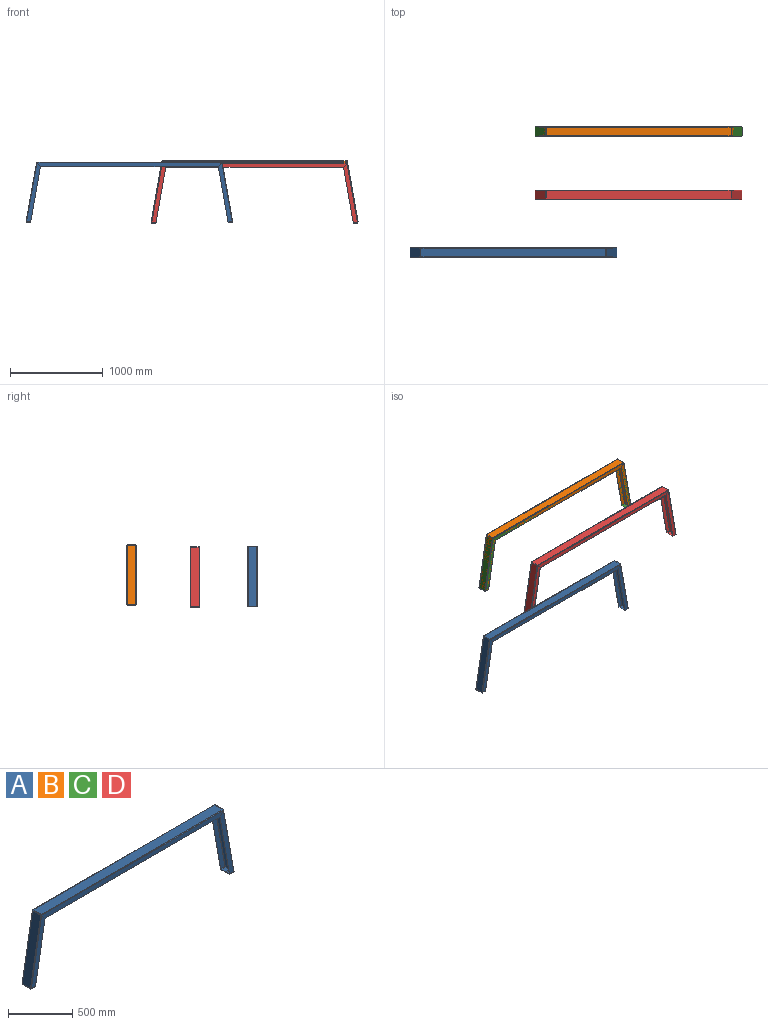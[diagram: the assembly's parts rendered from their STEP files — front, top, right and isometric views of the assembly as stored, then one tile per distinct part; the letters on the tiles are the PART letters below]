
ASSEMBLY  parts=4 mates=1
PART A: 130 faces, bbox 2234.1x100x650 mm
  f0: plane 3.37x2.87mm, normal (0,1,0), area 7.2mm2, adj f5,f11,f12,f83
  f1: plane 2.96x0.53mm, normal (0,-1,0), area 0mm2, adj f11,f12,f13,f75
  f2: plane 3.37x2.87mm, normal (0,-1,0), area 7.2mm2, adj f42,f48,f49,f66
  f3: plane 2.96x0.53mm, normal (0,1,0), area 0mm2, adj f48,f49,f51,f58
  f4: plane 2.95x2mm, normal (-0.17,0,0.98), area 6mm2, adj f8,f9,f11,f12
  f5: plane 2.95x2mm, normal (-0.17,0,0.98), area 6mm2, adj f0,f6,f11,f12
  f6: plane 3.52x3.48mm, normal (0,1,0), area 9.1mm2, adj f5,f10,f11,f12
  f7: plane 2.96x0.53mm, normal (0,1,0), area 0mm2, adj f11,f12,f14,f82
  f8: plane 3.37x2.87mm, normal (0,-1,0), area 7.2mm2, adj f4,f11,f12,f74
  f9: plane 3.52x3.48mm, normal (0,-1,0), area 9.1mm2, adj f4,f10,f11,f12
  f10: plane 94x2.95mm, normal (0.17,0,-0.98), area 282mm2, adj f6,f9,f11,f12
  f11: plane 645.35x113.79mm, normal (0.98,0,0.17), area 58989.4mm2, adj f0,f1,f4,f5,f6,f7,f8,f9
  f12: plane 645.35x113.79mm, normal (-0.98,0,-0.17), area 58989.4mm2, adj f0,f1,f4,f5,f6,f7,f8,f9
  f13: plane 4.92x4.65mm, normal (0,-1,0), area 14.7mm2, adj f1,f15,f16,f20
  f14: plane 4.92x4.65mm, normal (0,1,0), area 14.7mm2, adj f7,f15,f16,f17
  f15: cylinder r=5mm len=90mm, axis (0,-1,0), area 628.3mm2, adj f11,f13,f14,f21
  f16: cylinder r=2mm len=90mm, axis (0,-1,0), area 251.3mm2, adj f12,f13,f14,f22
  f17: plane 3x0.01mm, normal (0,1,0), area 0mm2, adj f14,f21,f22,f33
  f18: plane 3x0.01mm, normal (0,-1,0), area 0mm2, adj f21,f22,f29,f50
  f19: plane 3x0.01mm, normal (0,1,0), area 0mm2, adj f21,f22,f32,f51
  f20: plane 3x0.01mm, normal (0,-1,0), area 0mm2, adj f13,f21,f22,f28
  f21: plane 1996.64x90mm, normal (0,0,1), area 179697.9mm2, adj f15,f17,f18,f19,f20,f30,f34,f52
  f22: plane 1996.64x90mm, normal (0,0,-1), area 179697.9mm2, adj f16,f17,f18,f19,f20,f31,f35,f53
  f23: plane 1921.1x3mm, normal (0,0,-1), area 5763.3mm2, adj f24,f25,f26,f27
  f24: plane 45x37.76mm, normal (0.77,0,-0.64), area 176.2mm2, adj f23,f26,f27,f28
  f25: plane 45x37.76mm, normal (-0.77,0,-0.64), area 176.2mm2, adj f23,f26,f27,f29
  f26: plane 1996.62x45mm, normal (0,-1,0), area 88148.6mm2, adj f23,f24,f25,f30
  f27: plane 1996.62x45mm, normal (0,1,0), area 88148.6mm2, adj f23,f24,f25,f31
  f28: plane 5x5mm, normal (1,0,0), area 16.5mm2, adj f20,f24,f30,f31
  f29: plane 5x5mm, normal (-1,0,0), area 16.5mm2, adj f18,f25,f30,f31
  f30: cylinder r=5mm len=1996.62mm, axis (1,0,0), area 15681.4mm2, adj f21,f26,f28,f29
  f31: cylinder r=2mm len=1996.62mm, axis (1,0,0), area 6272.6mm2, adj f22,f27,f28,f29
  f32: plane 5x5mm, normal (-1,0,0), area 16.5mm2, adj f19,f34,f35,f37
  f33: plane 5x5mm, normal (1,0,0), area 16.5mm2, adj f17,f34,f35,f38
  f34: cylinder r=5mm len=1996.62mm, axis (-1,0,0), area 15681.4mm2, adj f21,f32,f33,f39
  f35: cylinder r=2mm len=1996.62mm, axis (-1,0,0), area 6272.6mm2, adj f22,f32,f33,f40
  f36: plane 1921.1x3mm, normal (0,0,-1), area 5763.3mm2, adj f37,f38,f39,f40
  f37: plane 45x37.76mm, normal (-0.77,0,-0.64), area 176.2mm2, adj f32,f36,f39,f40
  f38: plane 45x37.76mm, normal (0.77,0,-0.64), area 176.2mm2, adj f33,f36,f39,f40
  f39: plane 1996.62x45mm, normal (0,1,0), area 88148.6mm2, adj f34,f36,f37,f38
  f40: plane 1996.62x45mm, normal (0,-1,0), area 88148.6mm2, adj f35,f36,f37,f38
  f41: plane 2.95x2mm, normal (0.17,0,0.98), area 6mm2, adj f46,f47,f48,f49
  f42: plane 2.95x2mm, normal (0.17,0,0.98), area 6mm2, adj f2,f44,f48,f49
  f43: plane 94x2.95mm, normal (-0.17,0,-0.98), area 282mm2, adj f44,f47,f48,f49
  f44: plane 3.52x3.48mm, normal (0,-1,0), area 9.1mm2, adj f42,f43,f48,f49
  f45: plane 2.96x0.53mm, normal (0,-1,0), area 0mm2, adj f48,f49,f50,f67
  f46: plane 3.37x2.87mm, normal (0,1,0), area 7.2mm2, adj f41,f48,f49,f59
  f47: plane 3.52x3.48mm, normal (0,1,0), area 9.1mm2, adj f41,f43,f48,f49
  f48: plane 645.35x113.79mm, normal (-0.98,0,0.17), area 58989.4mm2, adj f2,f3,f41,f42,f43,f44,f45,f46
  f49: plane 645.35x113.79mm, normal (0.98,0,-0.17), area 58989.4mm2, adj f2,f3,f41,f42,f43,f44,f45,f46
  f50: plane 4.92x4.65mm, normal (0,-1,0), area 14.7mm2, adj f18,f45,f52,f53
  f51: plane 4.92x4.65mm, normal (0,1,0), area 14.7mm2, adj f3,f19,f52,f53
  f52: cylinder r=5mm len=90mm, axis (0,-1,0), area 628.3mm2, adj f21,f48,f50,f51
  f53: cylinder r=2mm len=90mm, axis (0,-1,0), area 251.3mm2, adj f22,f49,f50,f51
  f54: plane 45x37.76mm, normal (0.77,0,0.64), area 176.2mm2, adj f55,f56,f57,f58
  f55: plane 594.99x104.91mm, normal (0.98,0,-0.17), area 1812.5mm2, adj f54,f56,f57,f105
  f56: plane 639.99x150.61mm, normal (0,1,0), area 28215.6mm2, adj f54,f55,f60,f106
  f57: plane 639.99x150.61mm, normal (0,-1,0), area 28215.6mm2, adj f54,f55,f61,f107
  f58: plane 5x4.92mm, normal (0.17,0,0.98), area 16.5mm2, adj f3,f54,f60,f61
  f59: plane 5x4.92mm, normal (-0.17,0,-0.98), area 16.5mm2, adj f46,f60,f61,f104
  f60: cylinder r=5mm len=640.86mm, axis (0.17,0,0.98), area 5104mm2, adj f48,f56,f58,f59
  f61: cylinder r=2mm len=640.33mm, axis (0.17,0,0.98), area 2041.6mm2, adj f49,f57,f58,f59
  f62: plane 594.99x104.91mm, normal (0.98,0,-0.17), area 1812.5mm2, adj f63,f64,f65,f126
  f63: plane 45x37.76mm, normal (0.77,0,0.64), area 176.2mm2, adj f62,f64,f65,f67
  f64: plane 639.99x150.61mm, normal (0,-1,0), area 28215.6mm2, adj f62,f63,f68,f128
  f65: plane 639.99x150.61mm, normal (0,1,0), area 28215.6mm2, adj f62,f63,f69,f129
  f66: plane 5x4.92mm, normal (-0.17,0,-0.98), area 16.5mm2, adj f2,f68,f69,f127
  f67: plane 5x4.92mm, normal (0.17,0,0.98), area 16.5mm2, adj f45,f63,f68,f69
  f68: cylinder r=5mm len=640.86mm, axis (-0.17,0,-0.98), area 5104mm2, adj f48,f64,f66,f67
  f69: cylinder r=2mm len=640.33mm, axis (-0.17,0,-0.98), area 2041.6mm2, adj f49,f65,f66,f67
  f70: plane 45x37.76mm, normal (-0.77,0,0.64), area 176.2mm2, adj f71,f72,f73,f75
  f71: plane 594.99x104.91mm, normal (-0.98,0,-0.17), area 1812.5mm2, adj f70,f72,f73,f114
  f72: plane 639.99x150.61mm, normal (0,-1,0), area 28215.6mm2, adj f70,f71,f76,f115
  f73: plane 639.99x150.61mm, normal (0,1,0), area 28215.6mm2, adj f70,f71,f77,f116
  f74: plane 5x4.92mm, normal (0.17,0,-0.98), area 16.5mm2, adj f8,f76,f77,f113
  f75: plane 5x4.92mm, normal (-0.17,0,0.98), area 16.5mm2, adj f1,f70,f76,f77
  f76: cylinder r=5mm len=640.86mm, axis (0.17,0,-0.98), area 5104mm2, adj f11,f72,f74,f75
  f77: cylinder r=2mm len=640.33mm, axis (0.17,0,-0.98), area 2041.6mm2, adj f12,f73,f74,f75
  f78: plane 594.99x104.91mm, normal (-0.98,0,-0.17), area 1812.5mm2, adj f79,f80,f81,f91
  f79: plane 45x37.76mm, normal (-0.77,0,0.64), area 176.2mm2, adj f78,f80,f81,f82
  f80: plane 639.99x150.61mm, normal (0,1,0), area 28215.6mm2, adj f78,f79,f84,f93
  f81: plane 639.99x150.61mm, normal (0,-1,0), area 28215.6mm2, adj f78,f79,f85,f94
  f82: plane 5x4.92mm, normal (-0.17,0,0.98), area 16.5mm2, adj f7,f79,f84,f85
  f83: plane 5x4.92mm, normal (0.17,0,-0.98), area 16.5mm2, adj f0,f84,f85,f92
  f84: cylinder r=5mm len=640.86mm, axis (-0.17,0,0.98), area 5104mm2, adj f11,f80,f82,f83
  f85: cylinder r=2mm len=640.33mm, axis (-0.17,0,0.98), area 2041.6mm2, adj f12,f81,f82,f83
  f86: plane 45.34x3mm, normal (0,-1,0), area 136mm2, adj f87,f88,f89,f90
  f87: plane 44.99x3mm, normal (-1,0,0), area 135mm2, adj f86,f89,f90,f91
  f88: plane 44.99x3mm, normal (1,0,0), area 135mm2, adj f86,f89,f90,f92
  f89: plane 45.34x44.99mm, normal (0,0,-1), area 2039.9mm2, adj f86,f87,f88,f93
  f90: plane 45.34x44.99mm, normal (0,0,1), area 2039.9mm2, adj f86,f87,f88,f94
  f91: bspline ~5x5mm, area 16.6mm2, adj f78,f87,f93,f94
  f92: plane 5x5mm, normal (1,0,0), area 16.5mm2, adj f83,f88,f93,f94
  f93: cylinder r=5mm len=45.69mm, axis (-1,0,0), area 357.5mm2, adj f80,f89,f91,f92
  f94: cylinder r=2mm len=45.69mm, axis (-1,0,0), area 143mm2, adj f81,f90,f91,f92
  f95: plane 10x3mm, normal (0,-1,0), area 30mm2, adj f96,f101,f102,f103
  f96: plane 10x3mm, normal (1,0,0), area 30mm2, adj f95,f97,f102,f103
  f97: plane 10x3mm, normal (0,1,0), area 30mm2, adj f96,f101,f102,f103
  f98: plane 45.34x3mm, normal (0,-1,0), area 136mm2, adj f99,f100,f102,f103
  f99: plane 44.99x3mm, normal (-1,0,0), area 135mm2, adj f98,f102,f103,f104
  f100: plane 44.99x3mm, normal (1,0,0), area 135mm2, adj f98,f102,f103,f105
  f101: plane 10x3mm, normal (-1,0,0), area 30mm2, adj f95,f97,f102,f103
  f102: plane 45.34x44.99mm, normal (0,0,-1), area 1939.9mm2, adj f95,f96,f97,f98,f99,f100,f101,f106
  f103: plane 45.34x44.99mm, normal (0,0,1), area 1939.9mm2, adj f95,f96,f97,f98,f99,f100,f101,f107
  f104: plane 5x5mm, normal (-1,0,0), area 16.5mm2, adj f59,f99,f106,f107
  f105: bspline ~5x5mm, area 16.6mm2, adj f55,f100,f106,f107
  f106: cylinder r=5mm len=45.69mm, axis (-1,0,0), area 357.5mm2, adj f56,f102,f104,f105
  f107: cylinder r=2mm len=45.69mm, axis (-1,0,0), area 143mm2, adj f57,f103,f104,f105
  f108: plane 45.34x3mm, normal (0,1,0), area 136mm2, adj f109,f110,f111,f112
  f109: plane 44.99x3mm, normal (1,0,0), area 135mm2, adj f108,f111,f112,f113
  f110: plane 44.99x3mm, normal (-1,0,0), area 135mm2, adj f108,f111,f112,f114
  f111: plane 45.34x44.99mm, normal (0,0,-1), area 2039.9mm2, adj f108,f109,f110,f115
  f112: plane 45.34x44.99mm, normal (0,0,1), area 2039.9mm2, adj f108,f109,f110,f116
  f113: plane 5x5mm, normal (1,0,0), area 16.5mm2, adj f74,f109,f115,f116
  f114: bspline ~5x5mm, area 16.6mm2, adj f71,f110,f115,f116
  f115: cylinder r=5mm len=45.69mm, axis (1,0,0), area 357.5mm2, adj f72,f111,f113,f114
  f116: cylinder r=2mm len=45.69mm, axis (1,0,0), area 143mm2, adj f73,f112,f113,f114
  f117: plane 10x3mm, normal (-1,0,0), area 30mm2, adj f118,f123,f124,f125
  f118: plane 10x3mm, normal (0,-1,0), area 30mm2, adj f117,f119,f124,f125
  f119: plane 10x3mm, normal (1,0,0), area 30mm2, adj f118,f123,f124,f125
  f120: plane 45.34x3mm, normal (0,1,0), area 136mm2, adj f121,f122,f124,f125
  f121: plane 44.99x3mm, normal (1,0,0), area 135mm2, adj f120,f124,f125,f126
  f122: plane 44.99x3mm, normal (-1,0,0), area 135mm2, adj f120,f124,f125,f127
  f123: plane 10x3mm, normal (0,1,0), area 30mm2, adj f117,f119,f124,f125
  f124: plane 45.34x44.99mm, normal (0,0,-1), area 1939.9mm2, adj f117,f118,f119,f120,f121,f122,f123,f128
  f125: plane 45.34x44.99mm, normal (0,0,1), area 1939.9mm2, adj f117,f118,f119,f120,f121,f122,f123,f129
  f126: bspline ~5x5mm, area 16.6mm2, adj f62,f121,f128,f129
  f127: plane 5x5mm, normal (-1,0,0), area 16.5mm2, adj f66,f122,f128,f129
  f128: cylinder r=5mm len=45.69mm, axis (1,0,0), area 357.5mm2, adj f64,f124,f126,f127
  f129: cylinder r=2mm len=45.69mm, axis (1,0,0), area 143mm2, adj f65,f125,f126,f127
PART B: same geometry as A
PART C: same geometry as A
PART D: same geometry as A
PLACE A t=(-231.52,-395.46,136.76)mm
PLACE B t=(1121.55,911.54,150.31)mm
PLACE C t=(1121.55,911.54,150.31)mm
PLACE D t=(1121.55,226.7,130.07)mm
MATE planar B.f21 <-> C.f21  axis (0,0,1) through (0,861.54,842.68)mm
